# Revit family: Kühltische GN1-1 - Eigen
name_source: partatom
category: Sonderausstattung
revit_build: Autodesk Revit 2015 (Build: 20140606_1530(x64)
units: mm (PartAtom-declared; Revit-internal decimal feet)

## types (24) — shared parameters
Abstand Display seitlich = 60 mm  [stored 0.19685 ft]
Aufkantung Stärke = 6 mm  [stored 0.019685 ft]
Höhe Elektroanschluss = 150 mm
Korpus Tiefe = 620 mm
Kältemittel = R134a
Material = Edelstahl AISI 304
Pfosten Breite = 100 mm  [stored 0.328084 ft]
Pfosten Tiefe = 50 mm  [stored 0.164042 ft]
Platte Tiefe = 700 mm  [stored 2.29659 ft]
Pole = 1
Rückwand Stärke = 50 mm  [stored 0.164042 ft]
Scheinleistung = 0 VA
Seitenteilwand Stärke = 15 mm  [stored 0.0492126 ft]
Seitenwand Stärke = 50 mm  [stored 0.164042 ft]
Sockelhöhe = 150 mm
Spannung = 230 V
Temp. Bereich = -2°C bis +10°C
Tür_1 = Ja
Türen Stärke = 50 mm  [stored 0.164042 ft]
Wand oben Stärke = 50 mm  [stored 0.164042 ft]
Wand unten Stärke = 50 mm  [stored 0.164042 ft]
Öffnungstiefe = 470 mm  [stored 1.54199 ft]

## per-type parameters (varying)
- 435x1250 2-türig: Abstand Logo=158 mm; Artnr mit Platte=KTM 721142; Artnr mit Platte und Aufkantung=KTM 721141; Artnr ohne Platte=KTM 721140; Aufkantung Höhe=20 mm  [stored 0.0656168 ft]; Breite=1250 mm; Energieverbrauch=2,5 kWh/24 h; Kapazität=2 x 6 x GN 1/1; Korpus Breite=915 mm; Korpus Höhe=435 mm  [stored 1.42717 ft]; Kälteleistung=380 Watt -15°C VT/+32°C UT; Pfosten 1=Ja; Pfosten 2=Nein; Pfosten 3=Nein; Pfosten Abstand=440 mm; Pfosten Anzahl=1; Platte Stärke=20 mm  [stored 0.0656168 ft]; Seitenteil Breite=320 mm  [stored 1.04987 ft]; Tür_2=Ja; Tür_3=Nein; Tür_4=Nein; Türen Anzahl=2; Türen Breite=430 mm  [stored 1.41076 ft]; Türen Breite halb=215 mm  [stored 0.705381 ft]; Türen Höhe=415 mm  [stored 1.36155 ft]; Türen Lücke=20 mm  [stored 0.0656168 ft]; Versatz Tür zu Seitenteil=20 mm  [stored 0.0656168 ft]; Watt=460 W
- 435x1400 2-türig: Abstand Logo=158 mm; Artnr mit Platte=KTM 721142-C
KTM 721142-C; Artnr mit Platte und Aufkantung=KTM 721141-C; Artnr ohne Platte=KTM 721140-C; Aufkantung Höhe=20 mm  [stored 0.0656168 ft]; Breite=1400 mm; Energieverbrauch=2,5 kWh/24 h; Kapazität=2 x 6 x GN 1/1; Korpus Breite=1065 mm; Korpus Höhe=435 mm  [stored 1.42717 ft]; Kälteleistung=380 Watt -15°C VT/+32°C UT; Pfosten 1=Ja; Pfosten 2=Nein; Pfosten 3=Nein; Pfosten Abstand=515 mm  [stored 1.68963 ft]; Pfosten Anzahl=1; Platte Stärke=20 mm  [stored 0.0656168 ft]; Seitenteil Breite=320 mm  [stored 1.04987 ft]; Tür_2=Ja; Tür_3=Nein; Tür_4=Nein; Türen Anzahl=2; Türen Breite=505 mm  [stored 1.65682 ft]; Türen Breite halb=253 mm; Türen Höhe=415 mm  [stored 1.36155 ft]; Türen Lücke=20 mm  [stored 0.0656168 ft]; Versatz Tür zu Seitenteil=20 mm  [stored 0.0656168 ft]; Watt=460 W
- 435x1725 3-türig: Abstand Logo=158 mm; Artnr mit Platte=KTM 731142; Artnr mit Platte und Aufkantung=KTM 731141; Artnr ohne Platte=KTM 731140; Aufkantung Höhe=20 mm  [stored 0.0656168 ft]; Breite=1725 mm; Energieverbrauch=3,0 kWh/24 h; Kapazität=3 x 6 x GN 1/1; Korpus Breite=1390 mm; Korpus Höhe=435 mm  [stored 1.42717 ft]; Kälteleistung=380 Watt -15°C VT/+32°C UT; Pfosten 1=Ja; Pfosten 2=Ja; Pfosten 3=Nein; Pfosten Abstand=445 mm  [stored 1.45997 ft]; Pfosten Anzahl=2; Platte Stärke=20 mm  [stored 0.0656168 ft]; Seitenteil Breite=320 mm  [stored 1.04987 ft]; Tür_2=Ja; Tür_3=Ja; Tür_4=Nein; Türen Anzahl=3; Türen Breite=430 mm  [stored 1.41076 ft]; Türen Breite halb=215 mm  [stored 0.705381 ft]; Türen Höhe=415 mm  [stored 1.36155 ft]; Türen Lücke=30 mm  [stored 0.0984252 ft]; Versatz Tür zu Seitenteil=25 mm  [stored 0.082021 ft]; Watt=460 W
- 435x1800 3-türig: Abstand Logo=158 mm; Artnr mit Platte=KTM 731142-C; Artnr mit Platte und Aufkantung=KTM 731141-C; Artnr ohne Platte=KTM 731140-C; Aufkantung Höhe=20 mm  [stored 0.0656168 ft]; Breite=1800 mm; Energieverbrauch=3,0 kWh/24 h; Kapazität=3 x 6 x GN 1/1; Korpus Breite=1465 mm; Korpus Höhe=435 mm  [stored 1.42717 ft]; Kälteleistung=380 Watt -15°C VT/+32°C UT; Pfosten 1=Ja; Pfosten 2=Ja; Pfosten 3=Nein; Pfosten Abstand=470 mm  [stored 1.54199 ft]; Pfosten Anzahl=2; Platte Stärke=20 mm  [stored 0.0656168 ft]; Seitenteil Breite=320 mm  [stored 1.04987 ft]; Tür_2=Ja; Tür_3=Ja; Tür_4=Nein; Türen Anzahl=3; Türen Breite=455 mm; Türen Breite halb=228 mm  [stored 0.748031 ft]; Türen Höhe=415 mm  [stored 1.36155 ft]; Türen Lücke=30 mm  [stored 0.0984252 ft]; Versatz Tür zu Seitenteil=25 mm  [stored 0.082021 ft]; Watt=460 W
- 650x790 1-türig: Abstand Logo=265 mm; Artnr mit Platte=KTM 711162; Artnr mit Platte und Aufkantung=KTM 711161; Artnr ohne Platte=KTM 711160; Aufkantung Höhe=50 mm  [stored 0.164042 ft]; Breite=790 mm; Energieverbrauch=2,5 kWh/24 h; Kapazität=1 x 9 x GN1/1; Korpus Breite=445 mm  [stored 1.45997 ft]; Korpus Höhe=650 mm  [stored 2.13255 ft]; Kälteleistung=380 Watt -15°C VT/+32°C UT; Pfosten 1=Nein; Pfosten 2=Nein; Pfosten 3=Nein; Pfosten Abstand=400 mm  [stored 1.31234 ft]; Pfosten Anzahl=0; Platte Stärke=50 mm  [stored 0.164042 ft]; Seitenteil Breite=330 mm; Tür_2=Nein; Tür_3=Nein; Tür_4=Nein; Türen Anzahl=1; Türen Breite=390 mm  [stored 1.27953 ft]; Türen Breite halb=195 mm  [stored 0.639764 ft]; Türen Höhe=630 mm  [stored 2.06693 ft]; Türen Lücke=20 mm  [stored 0.0656168 ft]; Versatz Tür zu Seitenteil=40 mm  [stored 0.131234 ft]; Watt=440 W
- 650x1250 2-türig: Abstand Logo=265 mm; Artnr mit Platte=KTM 721162; Artnr mit Platte und Aufkantung=KTM 721161; Artnr ohne Platte=KTM 721160; Aufkantung Höhe=50 mm  [stored 0.164042 ft]; Breite=1250 mm; Energieverbrauch=2,7 kWh/24 h; Kapazität=2 x 9 x GN1/1; Korpus Breite=915 mm; Korpus Höhe=650 mm  [stored 2.13255 ft]; Kälteleistung=380 Watt -10°C VT/+32°C UT; Pfosten 1=Ja; Pfosten 2=Nein; Pfosten 3=Nein; Pfosten Abstand=440 mm; Pfosten Anzahl=1; Platte Stärke=50 mm  [stored 0.164042 ft]; Seitenteil Breite=320 mm  [stored 1.04987 ft]; Tür_2=Ja; Tür_3=Nein; Tür_4=Nein; Türen Anzahl=2; Türen Breite=430 mm  [stored 1.41076 ft]; Türen Breite halb=215 mm  [stored 0.705381 ft]; Türen Höhe=630 mm  [stored 2.06693 ft]; Türen Lücke=20 mm  [stored 0.0656168 ft]; Versatz Tür zu Seitenteil=20 mm  [stored 0.0656168 ft]; Watt=440 W
- 650x1725 3-türig: Abstand Logo=265 mm; Artnr mit Platte=KTM 731162
KTM 731162; Artnr mit Platte und Aufkantung=KTM 731161; Artnr ohne Platte=KTM 731160; Aufkantung Höhe=50 mm  [stored 0.164042 ft]; Breite=1725 mm; Energieverbrauch=3,2 kWh/24 h; Kapazität=3 x 9 x GN1/1; Korpus Breite=1390 mm; Korpus Höhe=650 mm  [stored 2.13255 ft]; Kälteleistung=380 Watt -15°C VT/+32°C UT; Pfosten 1=Ja; Pfosten 2=Ja; Pfosten 3=Nein; Pfosten Abstand=445 mm  [stored 1.45997 ft]; Pfosten Anzahl=2; Platte Stärke=50 mm  [stored 0.164042 ft]; Seitenteil Breite=320 mm  [stored 1.04987 ft]; Tür_2=Ja; Tür_3=Ja; Tür_4=Nein; Türen Anzahl=3; Türen Breite=430 mm  [stored 1.41076 ft]; Türen Breite halb=215 mm  [stored 0.705381 ft]; Türen Höhe=630 mm  [stored 2.06693 ft]; Türen Lücke=30 mm  [stored 0.0984252 ft]; Versatz Tür zu Seitenteil=25 mm  [stored 0.082021 ft]; Watt=460 W
- 650x2195 4-türig: Abstand Logo=265 mm; Artnr mit Platte=KTM 741162; Artnr mit Platte und Aufkantung=KTM 741161; Artnr ohne Platte=KTM 741160; Aufkantung Höhe=50 mm  [stored 0.164042 ft]; Breite=2195 mm; Energieverbrauch=3,5 kWh/24 h; Kapazität=4 x 9 x GN1/1; Korpus Breite=1860 mm; Korpus Höhe=650 mm  [stored 2.13255 ft]; Kälteleistung=380 Watt -15°C VT/+32°C UT; Pfosten 1=Ja; Pfosten 2=Ja; Pfosten 3=Ja; Pfosten Abstand=445 mm  [stored 1.45997 ft]; Pfosten Anzahl=3; Platte Stärke=50 mm  [stored 0.164042 ft]; Seitenteil Breite=320 mm  [stored 1.04987 ft]; Tür_2=Ja; Tür_3=Ja; Tür_4=Ja; Türen Anzahl=4; Türen Breite=430 mm  [stored 1.41076 ft]; Türen Breite halb=215 mm  [stored 0.705381 ft]; Türen Höhe=630 mm  [stored 2.06693 ft]; Türen Lücke=30 mm  [stored 0.0984252 ft]; Versatz Tür zu Seitenteil=35 mm  [stored 0.114829 ft]; Watt=480 W
- 700x790 1-türig: Abstand Logo=290 mm; Artnr mit Platte=KTM 711172-70; Artnr mit Platte und Aufkantung=KTM 711171-70; Artnr ohne Platte=KTM 711170-70; Aufkantung Höhe=50 mm  [stored 0.164042 ft]; Breite=790 mm; Energieverbrauch=2,55 kWh/24 h; Kapazität=1 x 10 x GN1/1; Korpus Breite=445 mm  [stored 1.45997 ft]; Korpus Höhe=700 mm  [stored 2.29659 ft]; Kälteleistung=380 Watt -15°C VT/+32°C UT; Pfosten 1=Nein; Pfosten 2=Nein; Pfosten 3=Nein; Pfosten Abstand=400 mm  [stored 1.31234 ft]; Pfosten Anzahl=0; Platte Stärke=50 mm  [stored 0.164042 ft]; Seitenteil Breite=330 mm; Tür_2=Nein; Tür_3=Nein; Tür_4=Nein; Türen Anzahl=1; Türen Breite=390 mm  [stored 1.27953 ft]; Türen Breite halb=195 mm  [stored 0.639764 ft]; Türen Höhe=680 mm  [stored 2.23097 ft]; Türen Lücke=20 mm  [stored 0.0656168 ft]; Versatz Tür zu Seitenteil=40 mm  [stored 0.131234 ft]; Watt=440 W
- 700x1250 2-türig: Abstand Logo=290 mm; Artnr mit Platte=KTM 721172-70; Artnr mit Platte und Aufkantung=KTM 721171-70; Artnr ohne Platte=KTM 721170-70; Aufkantung Höhe=50 mm  [stored 0.164042 ft]; Breite=1250 mm; Energieverbrauch=2,75 kWh/24 h; Kapazität=2 x 10 x GN1/1; Korpus Breite=915 mm; Korpus Höhe=700 mm  [stored 2.29659 ft]; Kälteleistung=380 Watt -10°C VT/+32°C UT; Pfosten 1=Ja; Pfosten 2=Nein; Pfosten 3=Nein; Pfosten Abstand=440 mm; Pfosten Anzahl=1; Platte Stärke=50 mm  [stored 0.164042 ft]; Seitenteil Breite=320 mm  [stored 1.04987 ft]; Tür_2=Ja; Tür_3=Nein; Tür_4=Nein; Türen Anzahl=2; Türen Breite=430 mm  [stored 1.41076 ft]; Türen Breite halb=215 mm  [stored 0.705381 ft]; Türen Höhe=680 mm  [stored 2.23097 ft]; Türen Lücke=20 mm  [stored 0.0656168 ft]; Versatz Tür zu Seitenteil=20 mm  [stored 0.0656168 ft]; Watt=440 W
- 700x1725 3-türig: Abstand Logo=290 mm; Artnr mit Platte=KTM 731172-70; Artnr mit Platte und Aufkantung=KTM 731171-70; Artnr ohne Platte=KTM 731170-70; Aufkantung Höhe=50 mm  [stored 0.164042 ft]; Breite=1725 mm; Energieverbrauch=3,25 kWh/24 h; Kapazität=3 x 10 x GN1/1; Korpus Breite=1390 mm; Korpus Höhe=700 mm  [stored 2.29659 ft]; Kälteleistung=380 Watt -15°C VT/+32°C UT; Pfosten 1=Ja; Pfosten 2=Ja; Pfosten 3=Nein; Pfosten Abstand=445 mm  [stored 1.45997 ft]; Pfosten Anzahl=2; Platte Stärke=50 mm  [stored 0.164042 ft]; Seitenteil Breite=320 mm  [stored 1.04987 ft]; Tür_2=Ja; Tür_3=Ja; Tür_4=Nein; Türen Anzahl=3; Türen Breite=430 mm  [stored 1.41076 ft]; Türen Breite halb=215 mm  [stored 0.705381 ft]; Türen Höhe=680 mm  [stored 2.23097 ft]; Türen Lücke=30 mm  [stored 0.0984252 ft]; Versatz Tür zu Seitenteil=25 mm  [stored 0.082021 ft]; Watt=460 W
- 700x2195 4-türig: Abstand Logo=290 mm; Artnr mit Platte=KTM 741172-70; Artnr mit Platte und Aufkantung=KTM 741171-70; Artnr ohne Platte=KTM 741170-70; Aufkantung Höhe=50 mm  [stored 0.164042 ft]; Breite=2195 mm; Energieverbrauch=3,55 kWh/24 h; Kapazität=4 x 10 x GN1/1; Korpus Breite=1860 mm; Korpus Höhe=700 mm  [stored 2.29659 ft]; Kälteleistung=380 Watt -15°C VT/+32°C UT; Pfosten 1=Ja; Pfosten 2=Ja; Pfosten 3=Ja; Pfosten Abstand=445 mm  [stored 1.45997 ft]; Pfosten Anzahl=3; Platte Stärke=50 mm  [stored 0.164042 ft]; Seitenteil Breite=320 mm  [stored 1.04987 ft]; Tür_2=Ja; Tür_3=Ja; Tür_4=Ja; Türen Anzahl=4; Türen Breite=430 mm  [stored 1.41076 ft]; Türen Breite halb=215 mm  [stored 0.705381 ft]; Türen Höhe=680 mm  [stored 2.23097 ft]; Türen Lücke=30 mm  [stored 0.0984252 ft]; Versatz Tür zu Seitenteil=35 mm  [stored 0.114829 ft]; Watt=480 W
- 710x790 1-türig: Abstand Logo=295 mm  [stored 0.967848 ft]; Artnr ohne Platte=KTM 711170-71; Aufkantung Höhe=50 mm  [stored 0.164042 ft]; Breite=790 mm; Energieverbrauch=2,55 kWh/24 h; Kapazität=1 x 10 x GN1/1; Korpus Breite=445 mm  [stored 1.45997 ft]; Korpus Höhe=710 mm; Kälteleistung=380 Watt -15°C VT/+32°C UT; Pfosten 1=Nein; Pfosten 2=Nein; Pfosten 3=Nein; Pfosten Abstand=400 mm  [stored 1.31234 ft]; Pfosten Anzahl=0; Platte Stärke=50 mm  [stored 0.164042 ft]; Seitenteil Breite=330 mm; Tür_2=Nein; Tür_3=Nein; Tür_4=Nein; Türen Anzahl=1; Türen Breite=390 mm  [stored 1.27953 ft]; Türen Breite halb=195 mm  [stored 0.639764 ft]; Türen Höhe=690 mm  [stored 2.26378 ft]; Türen Lücke=20 mm  [stored 0.0656168 ft]; Versatz Tür zu Seitenteil=40 mm  [stored 0.131234 ft]; Watt=440 W
- 710x1250 2-türig: Abstand Logo=295 mm  [stored 0.967848 ft]; Artnr ohne Platte=KTM 721170-71; Aufkantung Höhe=50 mm  [stored 0.164042 ft]; Breite=1250 mm; Energieverbrauch=2,75 kWh/24 h; Kapazität=2 x 10 x GN1/1; Korpus Breite=915 mm; Korpus Höhe=710 mm; Kälteleistung=380 Watt -10°C VT/+32°C UT; Pfosten 1=Ja; Pfosten 2=Nein; Pfosten 3=Nein; Pfosten Abstand=440 mm; Pfosten Anzahl=1; Platte Stärke=50 mm  [stored 0.164042 ft]; Seitenteil Breite=320 mm  [stored 1.04987 ft]; Tür_2=Ja; Tür_3=Nein; Tür_4=Nein; Türen Anzahl=2; Türen Breite=430 mm  [stored 1.41076 ft]; Türen Breite halb=215 mm  [stored 0.705381 ft]; Türen Höhe=690 mm  [stored 2.26378 ft]; Türen Lücke=20 mm  [stored 0.0656168 ft]; Versatz Tür zu Seitenteil=20 mm  [stored 0.0656168 ft]; Watt=440 W
- 710x1725 3-türig: Abstand Logo=295 mm  [stored 0.967848 ft]; Artnr ohne Platte=KTM 731170-71; Aufkantung Höhe=50 mm  [stored 0.164042 ft]; Breite=1725 mm; Energieverbrauch=3,25 kWh/24 h; Kapazität=3 x 10 x GN1/1; Korpus Breite=1390 mm; Korpus Höhe=710 mm; Kälteleistung=380 Watt -15°C VT/+32°C UT; Pfosten 1=Ja; Pfosten 2=Ja; Pfosten 3=Nein; Pfosten Abstand=445 mm  [stored 1.45997 ft]; Pfosten Anzahl=2; Platte Stärke=50 mm  [stored 0.164042 ft]; Seitenteil Breite=320 mm  [stored 1.04987 ft]; Tür_2=Ja; Tür_3=Ja; Tür_4=Nein; Türen Anzahl=3; Türen Breite=430 mm  [stored 1.41076 ft]; Türen Breite halb=215 mm  [stored 0.705381 ft]; Türen Höhe=690 mm  [stored 2.26378 ft]; Türen Lücke=30 mm  [stored 0.0984252 ft]; Versatz Tür zu Seitenteil=25 mm  [stored 0.082021 ft]; Watt=460 W
- 710x2195 4-türig: Abstand Logo=295 mm  [stored 0.967848 ft]; Artnr ohne Platte=KTM 741170-71; Aufkantung Höhe=50 mm  [stored 0.164042 ft]; Breite=2195 mm; Energieverbrauch=3,55 kWh/24 h; Kapazität=4 x 10 x GN1/1; Korpus Breite=1860 mm; Korpus Höhe=710 mm; Kälteleistung=380 Watt -15°C VT/+32°C UT; Pfosten 1=Ja; Pfosten 2=Ja; Pfosten 3=Ja; Pfosten Abstand=445 mm  [stored 1.45997 ft]; Pfosten Anzahl=3; Platte Stärke=50 mm  [stored 0.164042 ft]; Seitenteil Breite=320 mm  [stored 1.04987 ft]; Tür_2=Ja; Tür_3=Ja; Tür_4=Ja; Türen Anzahl=4; Türen Breite=430 mm  [stored 1.41076 ft]; Türen Breite halb=215 mm  [stored 0.705381 ft]; Türen Höhe=690 mm  [stored 2.26378 ft]; Türen Lücke=30 mm  [stored 0.0984252 ft]; Versatz Tür zu Seitenteil=35 mm  [stored 0.114829 ft]; Watt=480 W
- 750x2195 4-türig: Abstand Logo=315 mm  [stored 1.03346 ft]; Artnr mit Platte=KTM 741172; Artnr mit Platte und Aufkantung=KTM 741171; Artnr ohne Platte=KTM 741170; Aufkantung Höhe=50 mm  [stored 0.164042 ft]; Breite=2195 mm; Energieverbrauch=3,6 kWh/24 h; Kapazität=4 x 11 x GN1/1; Korpus Breite=1860 mm; Korpus Höhe=750 mm; Kälteleistung=380 Watt -15°C VT/+32°C UT; Pfosten 1=Ja; Pfosten 2=Ja; Pfosten 3=Ja; Pfosten Abstand=445 mm  [stored 1.45997 ft]; Pfosten Anzahl=3; Platte Stärke=50 mm  [stored 0.164042 ft]; Seitenteil Breite=320 mm  [stored 1.04987 ft]; Tür_2=Ja; Tür_3=Ja; Tür_4=Ja; Türen Anzahl=4; Türen Breite=430 mm  [stored 1.41076 ft]; Türen Breite halb=215 mm  [stored 0.705381 ft]; Türen Höhe=730 mm; Türen Lücke=30 mm  [stored 0.0984252 ft]; Versatz Tür zu Seitenteil=35 mm  [stored 0.114829 ft]; Watt=480 W
- 750x790 1-türig: Abstand Logo=315 mm  [stored 1.03346 ft]; Artnr mit Platte=KTM 711172; Artnr mit Platte und Aufkantung=KTM 711171; Artnr ohne Platte=KTM 711170; Aufkantung Höhe=50 mm  [stored 0.164042 ft]; Breite=790 mm; Energieverbrauch=2,6 kWh/24 h; Kapazität=1 x 11 x GN1/1; Korpus Breite=445 mm  [stored 1.45997 ft]; Korpus Höhe=750 mm; Kälteleistung=380 Watt -15°C VT/+32°C UT; Pfosten 1=Nein; Pfosten 2=Nein; Pfosten 3=Nein; Pfosten Abstand=400 mm  [stored 1.31234 ft]; Pfosten Anzahl=0; Platte Stärke=50 mm  [stored 0.164042 ft]; Seitenteil Breite=330 mm; Tür_2=Nein; Tür_3=Nein; Tür_4=Nein; Türen Anzahl=1; Türen Breite=390 mm  [stored 1.27953 ft]; Türen Breite halb=195 mm  [stored 0.639764 ft]; Türen Höhe=730 mm; Türen Lücke=20 mm  [stored 0.0656168 ft]; Versatz Tür zu Seitenteil=40 mm  [stored 0.131234 ft]; Watt=440 W
- 750x1725 3-türig: Abstand Logo=315 mm  [stored 1.03346 ft]; Artnr mit Platte=KTM 731172; Artnr mit Platte und Aufkantung=KTM 731171; Artnr ohne Platte=KTM 731170; Aufkantung Höhe=50 mm  [stored 0.164042 ft]; Breite=1725 mm; Energieverbrauch=3,3 kWh/24 h; Kapazität=3 x 11 x GN1/1; Korpus Breite=1390 mm; Korpus Höhe=750 mm; Kälteleistung=380 Watt -15°C VT/+32°C UT; Pfosten 1=Ja; Pfosten 2=Ja; Pfosten 3=Nein; Pfosten Abstand=445 mm  [stored 1.45997 ft]; Pfosten Anzahl=2; Platte Stärke=50 mm  [stored 0.164042 ft]; Seitenteil Breite=320 mm  [stored 1.04987 ft]; Tür_2=Ja; Tür_3=Ja; Tür_4=Nein; Türen Anzahl=3; Türen Breite=430 mm  [stored 1.41076 ft]; Türen Breite halb=215 mm  [stored 0.705381 ft]; Türen Höhe=730 mm; Türen Lücke=30 mm  [stored 0.0984252 ft]; Versatz Tür zu Seitenteil=25 mm  [stored 0.082021 ft]; Watt=460 W
- 750x1250 2-türig: Abstand Logo=315 mm  [stored 1.03346 ft]; Artnr mit Platte=KTM 721172; Artnr mit Platte und Aufkantung=KTM 721171; Artnr ohne Platte=KTM 721170; Aufkantung Höhe=50 mm  [stored 0.164042 ft]; Breite=1250 mm; Energieverbrauch=2,8 kWh/24 h; Kapazität=2 x 11 x GN1/1; Korpus Breite=915 mm; Korpus Höhe=750 mm; Kälteleistung=380 Watt -10°C VT/+32°C UT; Pfosten 1=Ja; Pfosten 2=Nein; Pfosten 3=Nein; Pfosten Abstand=440 mm; Pfosten Anzahl=1; Platte Stärke=50 mm  [stored 0.164042 ft]; Seitenteil Breite=320 mm  [stored 1.04987 ft]; Tür_2=Ja; Tür_3=Nein; Tür_4=Nein; Türen Anzahl=2; Türen Breite=430 mm  [stored 1.41076 ft]; Türen Breite halb=215 mm  [stored 0.705381 ft]; Türen Höhe=730 mm; Türen Lücke=20 mm  [stored 0.0656168 ft]; Versatz Tür zu Seitenteil=20 mm  [stored 0.0656168 ft]; Watt=440 W
- 760x790 1-türig: Abstand Logo=320 mm  [stored 1.04987 ft]; Artnr ohne Platte=KTM 711170-76; Aufkantung Höhe=50 mm  [stored 0.164042 ft]; Breite=790 mm; Energieverbrauch=2,6 kWh/24 h; Kapazität=1 x 11 x GN1/1; Korpus Breite=445 mm  [stored 1.45997 ft]; Korpus Höhe=760 mm; Kälteleistung=380 Watt -15°C VT/+32°C UT; Pfosten 1=Nein; Pfosten 2=Nein; Pfosten 3=Nein; Pfosten Abstand=400 mm  [stored 1.31234 ft]; Pfosten Anzahl=0; Platte Stärke=50 mm  [stored 0.164042 ft]; Seitenteil Breite=330 mm; Tür_2=Nein; Tür_3=Nein; Tür_4=Nein; Türen Anzahl=1; Türen Breite=390 mm  [stored 1.27953 ft]; Türen Breite halb=195 mm  [stored 0.639764 ft]; Türen Höhe=740 mm; Türen Lücke=20 mm  [stored 0.0656168 ft]; Versatz Tür zu Seitenteil=40 mm  [stored 0.131234 ft]; Watt=440 W
- 760x1250 2-türig: Abstand Logo=320 mm  [stored 1.04987 ft]; Artnr ohne Platte=KTM 721170-76; Aufkantung Höhe=50 mm  [stored 0.164042 ft]; Breite=1250 mm; Energieverbrauch=2,8 kWh/24 h; Kapazität=2 x 11 x GN1/1; Korpus Breite=915 mm; Korpus Höhe=760 mm; Kälteleistung=380 Watt -10°C VT/+32°C UT; Pfosten 1=Ja; Pfosten 2=Nein; Pfosten 3=Nein; Pfosten Abstand=440 mm; Pfosten Anzahl=1; Platte Stärke=50 mm  [stored 0.164042 ft]; Seitenteil Breite=320 mm  [stored 1.04987 ft]; Tür_2=Ja; Tür_3=Nein; Tür_4=Nein; Türen Anzahl=2; Türen Breite=430 mm  [stored 1.41076 ft]; Türen Breite halb=215 mm  [stored 0.705381 ft]; Türen Höhe=740 mm; Türen Lücke=20 mm  [stored 0.0656168 ft]; Versatz Tür zu Seitenteil=20 mm  [stored 0.0656168 ft]; Watt=440 W
- 760x1725 3-türig: Abstand Logo=320 mm  [stored 1.04987 ft]; Artnr ohne Platte=KTM 731170-76; Aufkantung Höhe=50 mm  [stored 0.164042 ft]; Breite=1725 mm; Energieverbrauch=3,3 kWh/24 h; Kapazität=3 x 11 x GN1/1; Korpus Breite=1390 mm; Korpus Höhe=760 mm; Kälteleistung=380 Watt -15°C VT/+32°C UT; Pfosten 1=Ja; Pfosten 2=Ja; Pfosten 3=Nein; Pfosten Abstand=445 mm  [stored 1.45997 ft]; Pfosten Anzahl=2; Platte Stärke=50 mm  [stored 0.164042 ft]; Seitenteil Breite=320 mm  [stored 1.04987 ft]; Tür_2=Ja; Tür_3=Ja; Tür_4=Nein; Türen Anzahl=3; Türen Breite=430 mm  [stored 1.41076 ft]; Türen Breite halb=215 mm  [stored 0.705381 ft]; Türen Höhe=740 mm; Türen Lücke=30 mm  [stored 0.0984252 ft]; Versatz Tür zu Seitenteil=25 mm  [stored 0.082021 ft]; Watt=460 W
- 760x2195 4-türig: Abstand Logo=320 mm  [stored 1.04987 ft]; Artnr ohne Platte=KTM 741170-76; Aufkantung Höhe=50 mm  [stored 0.164042 ft]; Breite=2195 mm; Energieverbrauch=3,6 kWh/24 h; Kapazität=4 x 11 x GN1/1; Korpus Breite=1860 mm; Korpus Höhe=760 mm; Kälteleistung=380 Watt -15°C VT/+32°C UT; Pfosten 1=Ja; Pfosten 2=Ja; Pfosten 3=Ja; Pfosten Abstand=445 mm  [stored 1.45997 ft]; Pfosten Anzahl=3; Platte Stärke=50 mm  [stored 0.164042 ft]; Seitenteil Breite=320 mm  [stored 1.04987 ft]; Tür_2=Ja; Tür_3=Ja; Tür_4=Ja; Türen Anzahl=4; Türen Breite=430 mm  [stored 1.41076 ft]; Türen Breite halb=215 mm  [stored 0.705381 ft]; Türen Höhe=740 mm; Türen Lücke=30 mm  [stored 0.0984252 ft]; Versatz Tür zu Seitenteil=35 mm  [stored 0.114829 ft]; Watt=480 W

note: [stored X ft] marks values corroborated as IEEE doubles in the binary element streams (Revit-internal decimal feet)

## geometry (parser evidence)
native form markers: Blend x14, Sweep x2
no freeform markers — native parametric forms only
